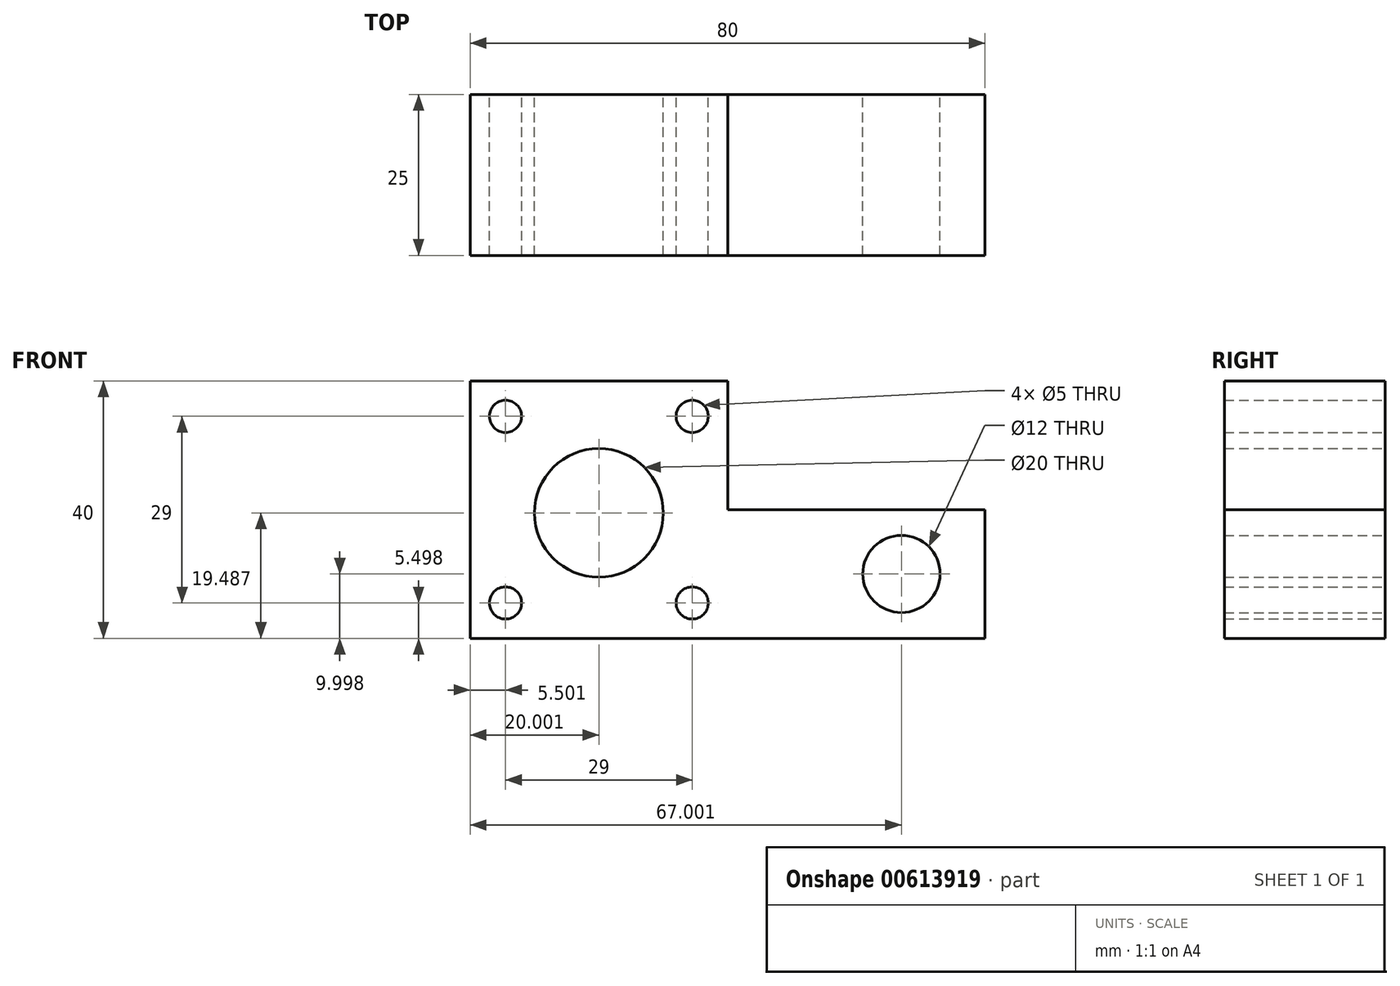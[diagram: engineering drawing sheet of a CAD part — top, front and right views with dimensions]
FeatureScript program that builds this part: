
annotation { "Feature Type Name" : "Feature", "Feature Type Description" : "" }
export const myFeature = defineFeature(function(context is Context, id is Id, definition is map)
    precondition{}
    {
        {
            var Q0;
            Q0=qCreatedBy(makeId("Front.planeOp"),FACE);
            var sketch = newSketch(context, id + "F0", { "sketchPlane" : qUnion([Q0])});
            skLineSegment(sketch, "E0", {"start": v(-60.8, 29.3) * mm, "end": v(-20.8, 29.3) * mm});
            skLineSegment(sketch, "E1", {"start": v(-20.8, 29.3) * mm, "end": v(-20.8, 9.3) * mm});
            skLineSegment(sketch, "E2", {"start": v(-20.8, 9.3) * mm, "end": v(19.2, 9.3) * mm});
            skLineSegment(sketch, "E3", {"start": v(19.2, 9.3) * mm, "end": v(19.2, -10.7) * mm});
            skLineSegment(sketch, "E4", {"start": v(19.2, -10.7) * mm, "end": v(-60.8, -10.7) * mm});
            skLineSegment(sketch, "E5", {"start": v(-60.8, -10.7) * mm, "end": v(-60.8, 29.3) * mm});
            skCircle(sketch, "E6", {"center": v(-40.8, 8.79) * mm, "radius": 10 * mm});
            skCircle(sketch, "E7", {"center": v(6.2, -0.7) * mm, "radius": 6 * mm});
            skPoint(sketch, "E7.centerSnap0", {"position": v(19.2, -0.7) * mm});
            skCircle(sketch, "E8", {"center": v(-55.3, 23.8) * mm, "radius": 2.5 * mm});
            skCircle(sketch, "E9", {"center": v(-26.3, 23.8) * mm, "radius": 2.5 * mm});
            skCircle(sketch, "E10", {"center": v(-26.3, -5.2) * mm, "radius": 2.5 * mm});
            skCircle(sketch, "E11", {"center": v(-55.3, -5.2) * mm, "radius": 2.5 * mm});
            skSolve(sketch);
        }
        {
            var Q0;
            Q0 = qSketchRegion(id + "F0", true);
            extrude(context, id + "F1", {"entities" : qUnion([Q0]), "depth" : 25 * mm, "offsetDistance" : 25 * mm});
        }
    });
